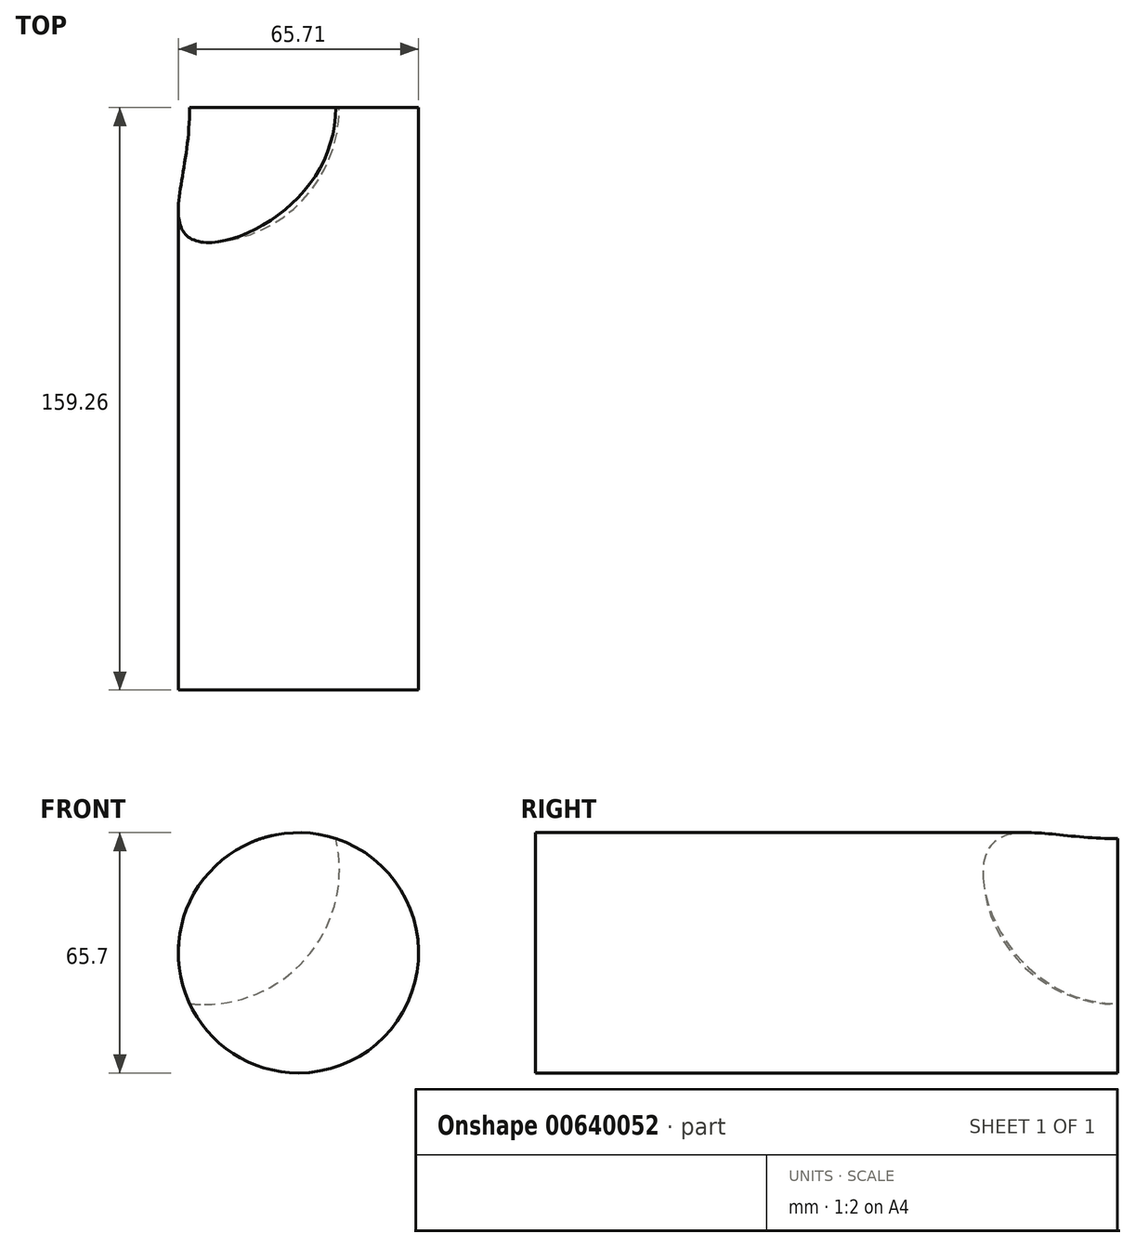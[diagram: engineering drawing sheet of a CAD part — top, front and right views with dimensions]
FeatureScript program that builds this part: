
annotation { "Feature Type Name" : "Feature", "Feature Type Description" : "" }
export const myFeature = defineFeature(function(context is Context, id is Id, definition is map)
    precondition{}
    {
        {
            var Q0;
            Q0=qCreatedBy(makeId("Front.planeOp"),FACE);
            var sketch = newSketch(context, id + "F0", { "sketchPlane" : qUnion([Q0])});
            skCircle(sketch, "E0", {"center": v(0, 0) * mm, "radius": 32.85 * mm});
            skSolve(sketch);
        }
        {
            var Q0;
            Q0=makeQuery(id+"F0.imprint","IMPRINT",FACE,{"disambiguationData":[TD([[makeQuery(id+"F0.imprint","IMPRINT",EDGE,{"derivedFrom":sQuery(id+"F0.wireOp",EDGE,"E0")}),1.0]])]});
            extrude(context, id + "F1", {"entities" : qUnion([Q0]), "depth" : 159.26 * mm, "offsetDistance" : 25.4 * mm});
        }
        {
            var Q0;
            Q0=qCreatedBy(makeId("Front.planeOp"),FACE);
            var sketch = newSketch(context, id + "F2", { "sketchPlane" : qUnion([Q0])});
            skArc(sketch, "E1", {"start": v(-25.74, -14.13) * mm, "mid": v(11.2, 22.8) * mm, "end": v(-25.74, 59.74) * mm});
            skLineSegment(sketch, "E2", {"start": v(-25.74, -14.13) * mm, "end": v(-25.74, 59.74) * mm});
            skSolve(sketch);
        }
        {
            var Q0;
            Q0=makeQuery(id+"F2.imprint","IMPRINT",FACE,{"disambiguationData":[TD([[makeQuery(id+"F2.imprint","IMPRINT",EDGE,{"derivedFrom":sQuery(id+"F2.wireOp",EDGE,"E1")}),1.0]])]});
            var Q1;
            Q1=sQuery(id+"F2.wireOp",EDGE,"E2");
            revolve(context, id + "F3", {"operationType" : NewBodyOperationType.ADD, "entities" : qUnion([Q0]), "axis" : qUnion([Q1]), "revolveType" : RevolveType.FULL});
        }
    });
